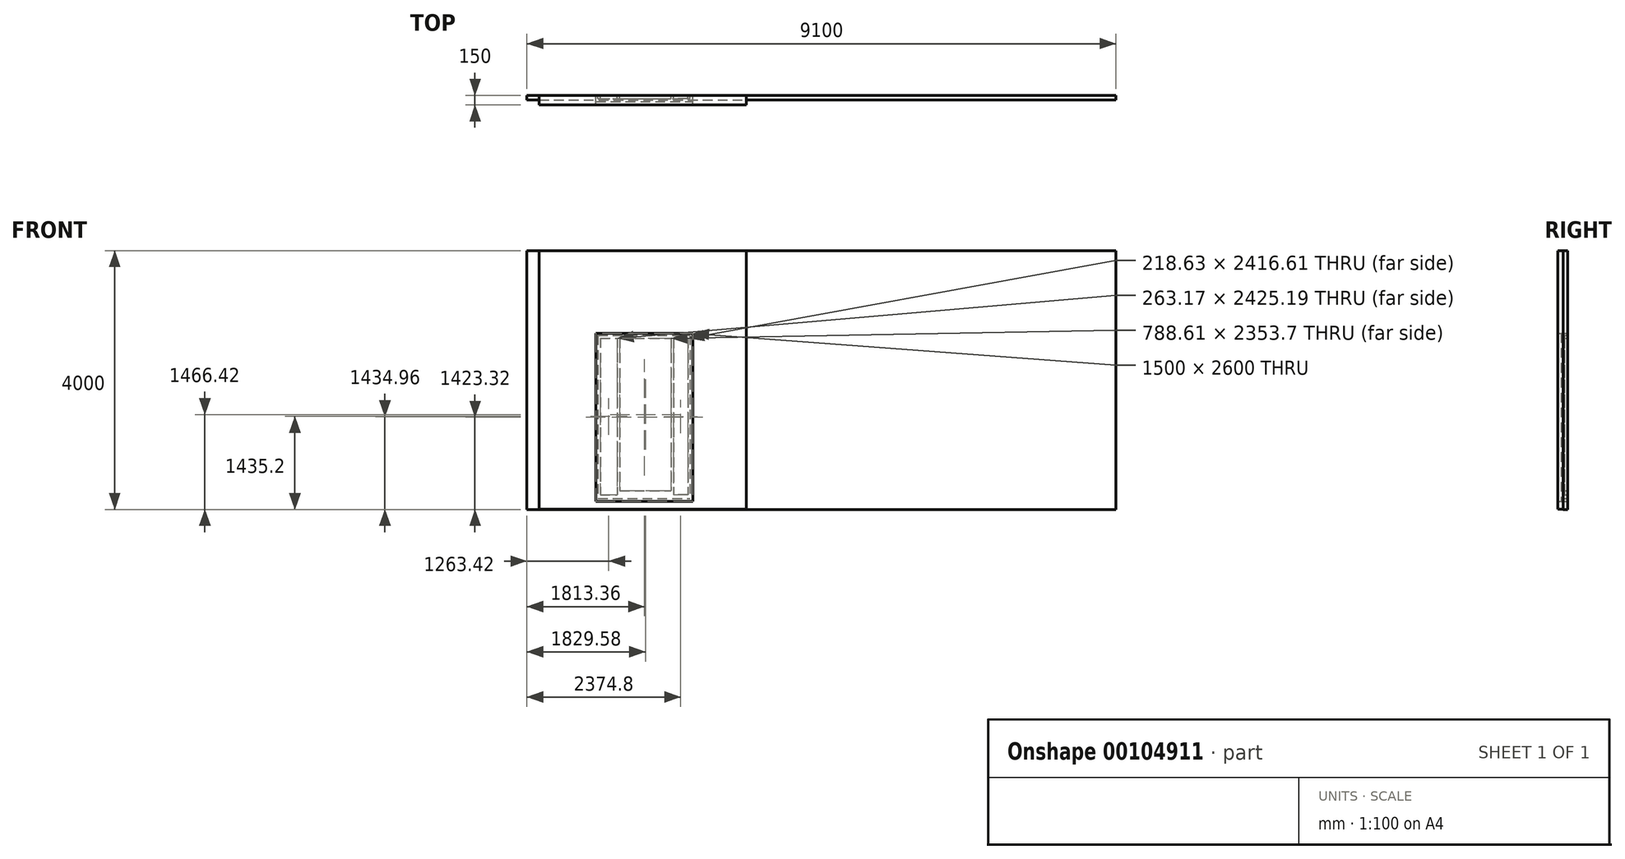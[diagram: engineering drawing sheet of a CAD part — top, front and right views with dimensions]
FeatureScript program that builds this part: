
annotation { "Feature Type Name" : "Feature", "Feature Type Description" : "" }
export const myFeature = defineFeature(function(context is Context, id is Id, definition is map)
    precondition{}
    {
        {
            var Q0;
            Q0=qCreatedBy(makeId("Front.planeOp"),FACE);
            var sketch = newSketch(context, id + "F0", { "sketchPlane" : qUnion([Q0])});
            skLineSegment(sketch, "E0.bottom", {"start": v(-2377.1, 3154.8) * mm, "end": v(6722.9, 3154.8) * mm});
            skLineSegment(sketch, "E0.top", {"start": v(-2377.1, -845.2) * mm, "end": v(6722.9, -845.2) * mm});
            skLineSegment(sketch, "E0.left", {"start": v(-2377.1, 3154.8) * mm, "end": v(-2377.1, -845.2) * mm});
            skLineSegment(sketch, "E0.right", {"start": v(6722.9, 3154.8) * mm, "end": v(6722.9, -845.2) * mm});
            skLineSegment(sketch, "E1.bottom", {"start": v(-2189.44, -842.5) * mm, "end": v(1010.56, -842.5) * mm});
            skLineSegment(sketch, "E1.top", {"start": v(-2189.44, 3157.5) * mm, "end": v(1010.56, 3157.5) * mm});
            skLineSegment(sketch, "E1.left", {"start": v(-2189.44, -842.5) * mm, "end": v(-2189.44, 3157.5) * mm});
            skLineSegment(sketch, "E1.right", {"start": v(1010.56, -842.5) * mm, "end": v(1010.56, 3157.5) * mm});
            skLineSegment(sketch, "E2.bottom", {"start": v(-1313.74, 1878.1) * mm, "end": v(186.26, 1878.1) * mm});
            skLineSegment(sketch, "E2.top", {"start": v(-1313.74, -721.9) * mm, "end": v(186.26, -721.9) * mm});
            skLineSegment(sketch, "E2.left", {"start": v(-1313.74, 1878.1) * mm, "end": v(-1313.74, -721.9) * mm});
            skLineSegment(sketch, "E2.right", {"start": v(186.26, 1878.1) * mm, "end": v(186.26, -721.9) * mm});
            skSolve(sketch);
        }
        {
            var Q0;
            Q0=makeQuery(id+"F0.imprint","IMPRINT",FACE,{"disambiguationData":[TD([[makeQuery(id+"F0.imprint","IMPRINT",EDGE,{"derivedFrom":sQuery(id+"F0.wireOp",EDGE,"E0.bottom")}),-1.0]])]});
            extrude(context, id + "F1", {"entities" : qUnion([Q0]), "depth" : 70 * mm});
        }
        {
            var Q0;
            Q0=makeQuery(id+"F0.imprint","IMPRINT",FACE,{"disambiguationData":[TD([[makeQuery(id+"F0.imprint","IMPRINT",EDGE,{"derivedFrom":sQuery(id+"F0.wireOp",EDGE,"E1.bottom")}),1.0]])]});
            extrude(context, id + "F2", {"entities" : qUnion([Q0]), "depth" : 150 * mm});
        }
        {
            var Q0;
            Q0=makeQuery(id+"F0.imprint","IMPRINT",FACE,{"disambiguationData":[TD([[makeQuery(id+"F0.imprint","IMPRINT",EDGE,{"derivedFrom":sQuery(id+"F0.wireOp",EDGE,"E2.bottom")}),-1.0]])]});
            extrude(context, id + "F3", {"entities" : qUnion([Q0]), "depth" : 100 * mm});
        }
        {
            var Q0;
            Q0=qCreatedBy(makeId("Front.planeOp"),FACE);
            var sketch = newSketch(context, id + "F4", { "sketchPlane" : qUnion([Q0])});
            skLineSegment(sketch, "E3.bottom", {"start": v(-1281.54, 1846.59) * mm, "end": v(144.03, 1846.59) * mm});
            skLineSegment(sketch, "E3.top", {"start": v(-1281.54, -676.97) * mm, "end": v(144.03, -676.97) * mm});
            skLineSegment(sketch, "E3.left", {"start": v(-1281.54, 1846.59) * mm, "end": v(-1281.54, -676.97) * mm});
            skLineSegment(sketch, "E3.right", {"start": v(144.03, 1846.59) * mm, "end": v(144.03, -676.97) * mm});
            skLineSegment(sketch, "E4.bottom", {"start": v(-941.83, 1798.06) * mm, "end": v(-153.22, 1798.06) * mm});
            skLineSegment(sketch, "E4.top", {"start": v(-941.83, -555.64) * mm, "end": v(-153.22, -555.64) * mm});
            skLineSegment(sketch, "E4.left", {"start": v(-941.83, 1798.06) * mm, "end": v(-941.83, -555.64) * mm});
            skLineSegment(sketch, "E4.right", {"start": v(-153.22, 1798.06) * mm, "end": v(-153.22, -555.64) * mm});
            skLineSegment(sketch, "E5.bottom", {"start": v(-1245.26, 1802.59) * mm, "end": v(-982.1, 1802.59) * mm});
            skLineSegment(sketch, "E5.top", {"start": v(-1245.26, -622.6) * mm, "end": v(-982.1, -622.6) * mm});
            skLineSegment(sketch, "E5.left", {"start": v(-1245.26, 1802.59) * mm, "end": v(-1245.26, -622.6) * mm});
            skLineSegment(sketch, "E5.right", {"start": v(-982.1, 1802.59) * mm, "end": v(-982.1, -622.6) * mm});
            skLineSegment(sketch, "E6.bottom", {"start": v(107.01, 1798.06) * mm, "end": v(-111.62, 1798.06) * mm});
            skLineSegment(sketch, "E6.top", {"start": v(107.01, -618.55) * mm, "end": v(-111.62, -618.55) * mm});
            skLineSegment(sketch, "E6.left", {"start": v(107.01, 1798.06) * mm, "end": v(107.01, -618.55) * mm});
            skLineSegment(sketch, "E6.right", {"start": v(-111.62, 1798.06) * mm, "end": v(-111.62, -618.55) * mm});
            skLineSegment(sketch, "E7.bottom", {"start": v(-1245.26, 806.6) * mm, "end": v(-982.1, 806.6) * mm});
            skLineSegment(sketch, "E7.top", {"start": v(-1245.26, 478.65) * mm, "end": v(-982.1, 478.65) * mm});
            skLineSegment(sketch, "E7.left", {"start": v(-1245.26, 806.6) * mm, "end": v(-1245.26, 478.65) * mm});
            skLineSegment(sketch, "E7.right", {"start": v(-982.1, 806.6) * mm, "end": v(-982.1, 478.65) * mm});
            skLineSegment(sketch, "E8.bottom", {"start": v(-111.62, 851.14) * mm, "end": v(107.01, 851.14) * mm});
            skLineSegment(sketch, "E8.top", {"start": v(-111.62, 470.55) * mm, "end": v(107.01, 470.55) * mm});
            skLineSegment(sketch, "E8.left", {"start": v(-111.62, 851.14) * mm, "end": v(-111.62, 470.55) * mm});
            skLineSegment(sketch, "E8.right", {"start": v(107.01, 851.14) * mm, "end": v(107.01, 470.55) * mm});
            skSolve(sketch);
        }
        {
            var Q0;
            Q0=qSketchRegion(id+"F4",true);
            extrude(context, id + "F5", {"entities" : qUnion([Q0]), "depth" : 50 * mm});
        }
    });
